# Revit family: CRAWFORD_IndustrialDoor_1142P
name_source: partatom
category: Doors
units: mm (PartAtom-declared; Revit-internal decimal feet)

## family parameters
Always vertical = Yes
Cut with Voids When Loaded = No
Host = Wall
Room Calculation Point = No
Shared = No

## types (2) — shared parameters
Analytic Construction = <None>
ControlBoxDepth = 120 mm
ControlBoxLength = 380 mm
ControlBoxWidth = 180 mm
DaylightHeightMax = 3600 mm  [stored 11.811 ft]
DaylightHeightMin = 1800 mm  [stored 5.90551 ft]
Description = Overhead Sectional Door
InclinationOfHorizontaltrackMax = 45.00°
Manufacturer = CRAWFORD
Model = OH1142P
PanelHeightMiddle = 545 mm  [stored 1.78806 ft]
TracksetLiftHigh = TracksetLift : High lift
TracksetLiftVertical = TracksetVerticalLift : Trackset Vertical lift

## per-type parameters (varying)
| type | TracksetType | URL |
| Vertical lift | TracksetVerticalLift : Trackset Vertical lift |  |
| High lift | TracksetLift : High lift | https://www.assaabloyentrance.com |

note: [stored X ft] marks values corroborated as IEEE doubles in the binary element streams (Revit-internal decimal feet)

## geometry (parser evidence)
native form markers: Sweep x34
no freeform markers — native parametric forms only
